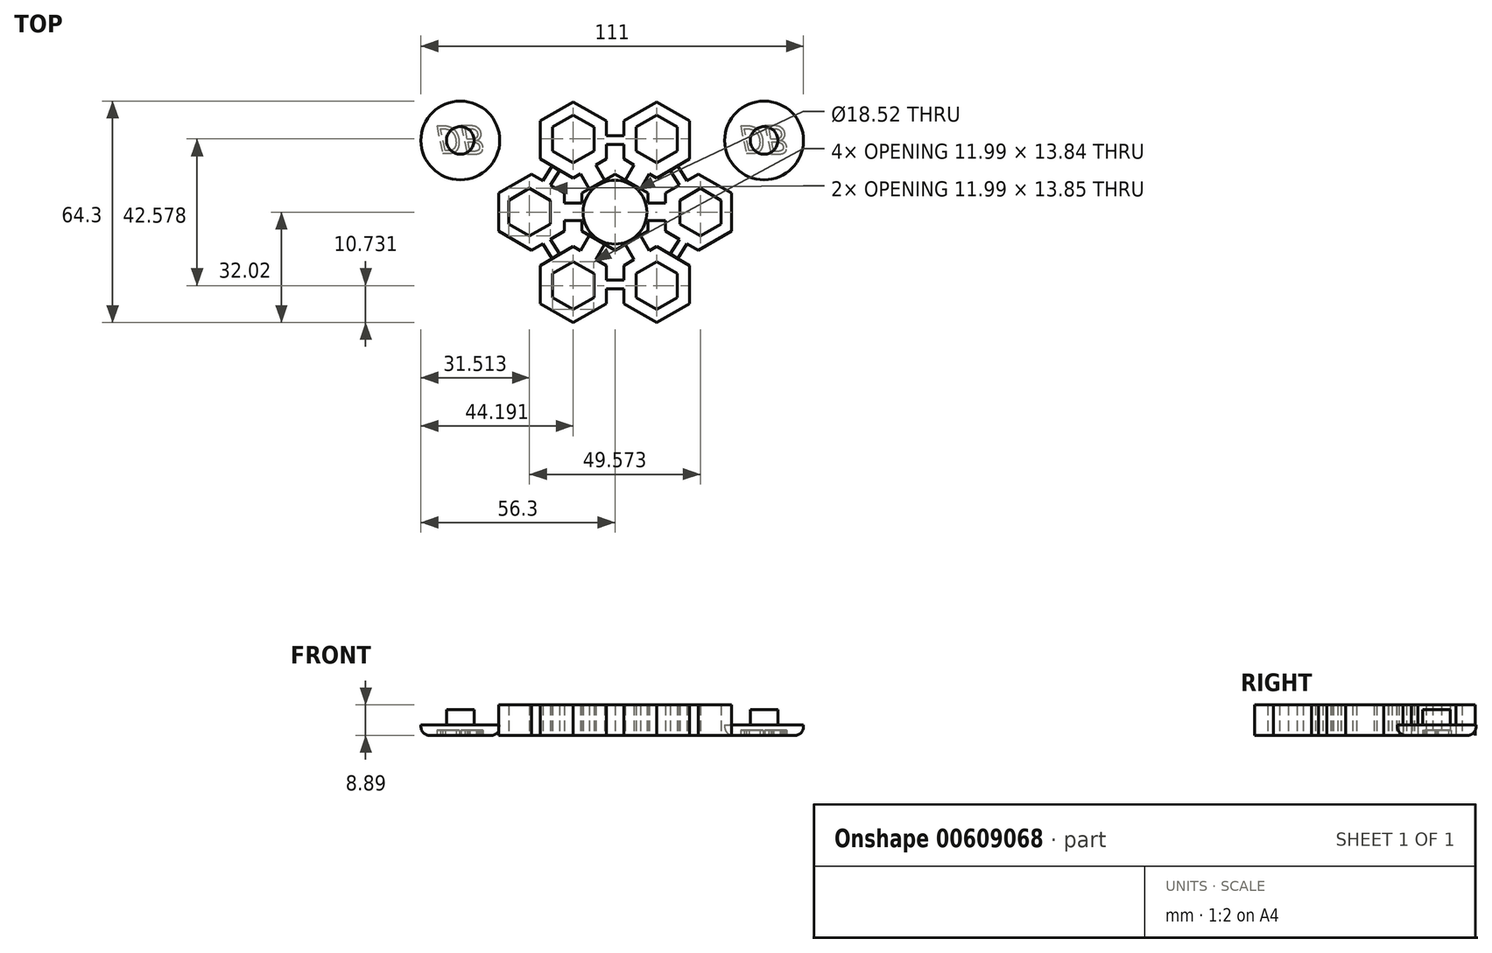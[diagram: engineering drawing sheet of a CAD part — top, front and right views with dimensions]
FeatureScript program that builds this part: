
annotation { "Feature Type Name" : "Feature", "Feature Type Description" : "" }
export const myFeature = defineFeature(function(context is Context, id is Id, definition is map)
    precondition{}
    {
        {
            var Q0;
            Q0=qCreatedBy(makeId("Top.planeOp"),FACE);
            var sketch = newSketch(context, id + "F0", { "sketchPlane" : qUnion([Q0])});
            skCircle(sketch, "E0.cCircle", {"center": v(0, 0) * mm, "radius": 9.57 * mm, "construction": true});
            skLineSegment(sketch, "E0.0", {"start": v(9.57, -5.52) * mm, "end": v(0, -11.05) * mm});
            skLineSegment(sketch, "E0.1", {"start": v(0, -11.05) * mm, "end": v(-9.57, -5.52) * mm});
            skLineSegment(sketch, "E0.2", {"start": v(-9.57, -5.52) * mm, "end": v(-9.57, 5.52) * mm});
            skLineSegment(sketch, "E0.3", {"start": v(-9.57, 5.52) * mm, "end": v(0, 11.05) * mm});
            skLineSegment(sketch, "E0.4", {"start": v(0, 11.05) * mm, "end": v(9.57, 5.52) * mm});
            skLineSegment(sketch, "E0.5", {"start": v(9.57, 5.52) * mm, "end": v(9.57, -5.52) * mm});
            skPoint(sketch, "E0.0.midPoint", {"position": v(4.78, -8.29) * mm});
            skCircle(sketch, "E1.cCircle", {"center": v(-12.1, 20.97) * mm, "radius": 9.57 * mm, "construction": true});
            skLineSegment(sketch, "E1.0", {"start": v(-2.54, 26.5) * mm, "end": v(-2.54, 15.45) * mm});
            skLineSegment(sketch, "E1.1", {"start": v(-2.54, 15.45) * mm, "end": v(-12.1, 9.92) * mm});
            skLineSegment(sketch, "E1.2", {"start": v(-12.1, 9.92) * mm, "end": v(-21.68, 15.45) * mm});
            skLineSegment(sketch, "E1.3", {"start": v(-21.68, 15.45) * mm, "end": v(-21.68, 26.5) * mm});
            skLineSegment(sketch, "E1.4", {"start": v(-21.68, 26.5) * mm, "end": v(-12.1, 32.02) * mm});
            skLineSegment(sketch, "E1.5", {"start": v(-12.1, 32.02) * mm, "end": v(-2.54, 26.5) * mm});
            skCircle(sketch, "E2.cCircle", {"center": v(-24.22, 0) * mm, "radius": 9.57 * mm, "construction": true});
            skLineSegment(sketch, "E2.0", {"start": v(-14.65, 5.52) * mm, "end": v(-14.65, -5.52) * mm});
            skLineSegment(sketch, "E2.1", {"start": v(-14.65, -5.52) * mm, "end": v(-24.22, -11.05) * mm});
            skLineSegment(sketch, "E2.2", {"start": v(-24.22, -11.05) * mm, "end": v(-33.79, -5.52) * mm});
            skLineSegment(sketch, "E2.3", {"start": v(-33.79, -5.52) * mm, "end": v(-33.79, 5.52) * mm});
            skLineSegment(sketch, "E2.4", {"start": v(-33.79, 5.52) * mm, "end": v(-24.22, 11.05) * mm});
            skLineSegment(sketch, "E2.5", {"start": v(-24.22, 11.05) * mm, "end": v(-14.65, 5.52) * mm});
            skPoint(sketch, "E2.0.midPoint", {"position": v(-14.65, 0) * mm});
            skCircle(sketch, "E3.cCircle", {"center": v(-12.1, -20.97) * mm, "radius": 9.57 * mm, "construction": true});
            skLineSegment(sketch, "E3.0", {"start": v(-2.54, -26.5) * mm, "end": v(-12.1, -32.02) * mm});
            skLineSegment(sketch, "E3.1", {"start": v(-12.1, -32.02) * mm, "end": v(-21.68, -26.5) * mm});
            skLineSegment(sketch, "E3.2", {"start": v(-21.68, -26.5) * mm, "end": v(-21.68, -15.45) * mm});
            skLineSegment(sketch, "E3.3", {"start": v(-21.68, -15.45) * mm, "end": v(-12.1, -9.92) * mm});
            skLineSegment(sketch, "E3.4", {"start": v(-12.1, -9.92) * mm, "end": v(-2.54, -15.45) * mm});
            skLineSegment(sketch, "E3.5", {"start": v(-2.54, -15.45) * mm, "end": v(-2.54, -26.5) * mm});
            skLineSegment(sketch, "E4.MirrorCS", {"start": v(21.68, 26.5) * mm, "end": v(12.1, 32.02) * mm});
            skLineSegment(sketch, "E5.MirrorCS", {"start": v(21.68, 15.45) * mm, "end": v(21.68, 26.5) * mm});
            skLineSegment(sketch, "E6.MirrorCS", {"start": v(12.1, 9.92) * mm, "end": v(21.68, 15.45) * mm});
            skLineSegment(sketch, "E7.MirrorCS", {"start": v(2.54, 15.45) * mm, "end": v(12.1, 9.92) * mm});
            skLineSegment(sketch, "E8.MirrorCS", {"start": v(2.54, 26.5) * mm, "end": v(2.54, 15.45) * mm});
            skLineSegment(sketch, "E9.MirrorCS", {"start": v(12.1, 32.02) * mm, "end": v(2.54, 26.5) * mm});
            skCircle(sketch, "E10.MirrorC", {"center": v(12.1, 20.97) * mm, "radius": 9.57 * mm, "construction": true});
            skLineSegment(sketch, "E11.MirrorCS", {"start": v(24.22, 11.05) * mm, "end": v(14.65, 5.52) * mm});
            skLineSegment(sketch, "E12.MirrorCS", {"start": v(33.79, 5.52) * mm, "end": v(24.22, 11.05) * mm});
            skLineSegment(sketch, "E13.MirrorCS", {"start": v(33.79, -5.52) * mm, "end": v(33.79, 5.52) * mm});
            skLineSegment(sketch, "E14.MirrorCS", {"start": v(24.22, -11.05) * mm, "end": v(33.79, -5.52) * mm});
            skLineSegment(sketch, "E15.MirrorCS", {"start": v(14.65, -5.52) * mm, "end": v(24.22, -11.05) * mm});
            skLineSegment(sketch, "E16.MirrorCS", {"start": v(14.65, 5.52) * mm, "end": v(14.65, -5.52) * mm});
            skCircle(sketch, "E17.MirrorC", {"center": v(24.22, 0) * mm, "radius": 9.57 * mm, "construction": true});
            skLineSegment(sketch, "E18.MirrorCS", {"start": v(2.54, -15.45) * mm, "end": v(2.54, -26.5) * mm});
            skLineSegment(sketch, "E19.MirrorCS", {"start": v(12.1, -9.92) * mm, "end": v(2.54, -15.45) * mm});
            skLineSegment(sketch, "E20.MirrorCS", {"start": v(21.68, -15.45) * mm, "end": v(12.1, -9.92) * mm});
            skLineSegment(sketch, "E21.MirrorCS", {"start": v(21.68, -26.5) * mm, "end": v(21.68, -15.45) * mm});
            skLineSegment(sketch, "E22.MirrorCS", {"start": v(12.1, -32.02) * mm, "end": v(21.68, -26.5) * mm});
            skLineSegment(sketch, "E23.MirrorCS", {"start": v(2.54, -26.5) * mm, "end": v(12.1, -32.02) * mm});
            skCircle(sketch, "E24.MirrorC", {"center": v(12.1, -20.97) * mm, "radius": 9.57 * mm, "construction": true});
            skLineSegment(sketch, "E25.bottom", {"start": v(-14.65, 2.67) * mm, "end": v(-9.57, 2.67) * mm});
            skLineSegment(sketch, "E25.top", {"start": v(-14.65, -2.41) * mm, "end": v(-9.57, -2.41) * mm});
            skLineSegment(sketch, "E25.left", {"start": v(-14.65, 2.67) * mm, "end": v(-14.65, -2.41) * mm});
            skLineSegment(sketch, "E25.right", {"start": v(-9.57, 2.67) * mm, "end": v(-9.57, -2.41) * mm});
            skLineSegment(sketch, "E26.MirrorCS", {"start": v(14.65, 2.67) * mm, "end": v(9.57, 2.67) * mm});
            skLineSegment(sketch, "E27.MirrorCS", {"start": v(14.65, -2.41) * mm, "end": v(9.57, -2.41) * mm});
            skLineSegment(sketch, "E28.MirrorCS", {"start": v(9.57, 2.67) * mm, "end": v(9.57, -2.41) * mm});
            skLineSegment(sketch, "E29.bottom", {"start": v(-9.96, 11.17) * mm, "end": v(-5.56, 13.7) * mm});
            skLineSegment(sketch, "E29.top", {"start": v(-7.42, 6.77) * mm, "end": v(-3.02, 9.3) * mm});
            skLineSegment(sketch, "E29.left", {"start": v(-9.96, 11.17) * mm, "end": v(-7.42, 6.77) * mm});
            skLineSegment(sketch, "E29.right", {"start": v(-5.56, 13.7) * mm, "end": v(-3.02, 9.3) * mm});
            skLineSegment(sketch, "E30.MirrorCS", {"start": v(-9.57, -5.52) * mm, "end": v(0, -11.05) * mm});
            skLineSegment(sketch, "E31.bottom", {"start": v(-2.54, -19.7) * mm, "end": v(2.54, -19.7) * mm});
            skLineSegment(sketch, "E31.top", {"start": v(-2.54, -22.24) * mm, "end": v(2.54, -22.24) * mm});
            skLineSegment(sketch, "E31.left", {"start": v(-2.54, -19.7) * mm, "end": v(-2.54, -22.24) * mm});
            skLineSegment(sketch, "E31.right", {"start": v(2.54, -19.7) * mm, "end": v(2.54, -22.24) * mm});
            skLineSegment(sketch, "E32.MirrorCS", {"start": v(9.96, 11.17) * mm, "end": v(7.42, 6.77) * mm});
            skLineSegment(sketch, "E33.MirrorCS", {"start": v(9.96, 11.17) * mm, "end": v(5.56, 13.7) * mm});
            skLineSegment(sketch, "E34.MirrorCS", {"start": v(5.56, 13.7) * mm, "end": v(3.02, 9.3) * mm});
            skLineSegment(sketch, "E35.MirrorCS", {"start": v(9.57, 5.52) * mm, "end": v(0, 11.05) * mm});
            skLineSegment(sketch, "E36", {"start": v(3.02, 9.3) * mm, "end": v(7.42, 6.77) * mm});
            skLineSegment(sketch, "E37.MirrorCS", {"start": v(-9.96, -11.17) * mm, "end": v(-7.42, -6.77) * mm});
            skLineSegment(sketch, "E38.MirrorCS", {"start": v(-5.56, -13.7) * mm, "end": v(-3.02, -9.3) * mm});
            skLineSegment(sketch, "E39.MirrorCS", {"start": v(-9.96, -11.17) * mm, "end": v(-5.56, -13.7) * mm});
            skLineSegment(sketch, "E40.MirrorCS", {"start": v(-7.42, -6.77) * mm, "end": v(-3.02, -9.3) * mm});
            skLineSegment(sketch, "E41.MirrorCS", {"start": v(9.96, -11.17) * mm, "end": v(7.42, -6.77) * mm});
            skLineSegment(sketch, "E42.MirrorCS", {"start": v(5.56, -13.7) * mm, "end": v(3.02, -9.3) * mm});
            skLineSegment(sketch, "E43", {"start": v(5.56, 13.7) * mm, "end": v(9.96, 11.17) * mm});
            skLineSegment(sketch, "E44.MirrorCS", {"start": v(5.56, -13.7) * mm, "end": v(9.96, -11.17) * mm});
            skLineSegment(sketch, "E45", {"start": v(3.02, -9.3) * mm, "end": v(7.42, -6.77) * mm});
            skLineSegment(sketch, "E46.MirrorCS", {"start": v(-2.54, 19.7) * mm, "end": v(2.54, 19.7) * mm});
            skLineSegment(sketch, "E47.MirrorCS", {"start": v(2.54, 19.7) * mm, "end": v(2.54, 22.24) * mm});
            skLineSegment(sketch, "E48.MirrorCS", {"start": v(-2.54, 19.7) * mm, "end": v(-2.54, 22.24) * mm});
            skLineSegment(sketch, "E49.MirrorCS", {"start": v(-2.54, 22.24) * mm, "end": v(2.54, 22.24) * mm});
            skLineSegment(sketch, "E50.bottom", {"start": v(-20.9, 9.14) * mm, "end": v(-18.21, 13.44) * mm});
            skLineSegment(sketch, "E50.top", {"start": v(-18.76, 7.79) * mm, "end": v(-16.06, 12.1) * mm});
            skLineSegment(sketch, "E50.left", {"start": v(-20.9, 9.14) * mm, "end": v(-18.76, 7.79) * mm});
            skLineSegment(sketch, "E50.right", {"start": v(-18.21, 13.44) * mm, "end": v(-16.06, 12.1) * mm});
            skLineSegment(sketch, "E51.0", {"start": v(-20.9, 9.14) * mm, "end": v(-18.21, 13.44) * mm, "construction": true});
            skLineSegment(sketch, "E51.1", {"start": v(-20.9, 9.14) * mm, "end": v(-20.9, 9.14) * mm});
            skLineSegment(sketch, "E52.MirrorCS", {"start": v(20.9, 9.14) * mm, "end": v(18.21, 13.44) * mm});
            skLineSegment(sketch, "E53.MirrorCS", {"start": v(18.21, 13.44) * mm, "end": v(16.06, 12.1) * mm});
            skLineSegment(sketch, "E54.MirrorCS", {"start": v(18.76, 7.79) * mm, "end": v(16.06, 12.1) * mm});
            skLineSegment(sketch, "E55.MirrorCS", {"start": v(20.9, 9.14) * mm, "end": v(18.76, 7.79) * mm});
            skLineSegment(sketch, "E56.MirrorCS", {"start": v(-20.9, -9.14) * mm, "end": v(-18.21, -13.44) * mm});
            skLineSegment(sketch, "E57.MirrorCS", {"start": v(-18.76, -7.79) * mm, "end": v(-16.06, -12.1) * mm});
            skLineSegment(sketch, "E58.MirrorCS", {"start": v(-18.21, -13.44) * mm, "end": v(-16.06, -12.1) * mm});
            skLineSegment(sketch, "E59.MirrorCS", {"start": v(-20.9, -9.14) * mm, "end": v(-18.76, -7.79) * mm});
            skLineSegment(sketch, "E60.MirrorCS", {"start": v(18.76, -7.79) * mm, "end": v(16.06, -12.1) * mm});
            skLineSegment(sketch, "E61.MirrorCS", {"start": v(20.9, -9.14) * mm, "end": v(18.76, -7.79) * mm});
            skLineSegment(sketch, "E62.MirrorCS", {"start": v(20.9, -9.14) * mm, "end": v(18.21, -13.44) * mm});
            skLineSegment(sketch, "E63.MirrorCS", {"start": v(18.21, -13.44) * mm, "end": v(16.06, -12.1) * mm});
            skCircle(sketch, "E64", {"center": v(0, 0) * mm, "radius": 9.26 * mm});
            skSolve(sketch);
        }
        {
            var Q0;
            Q0 = qSketchRegion(id + "F0", true);
            extrude(context, id + "F1", {"entities" : qUnion([Q0]), "depth" : 8.9 * mm, "offsetDistance" : 25.4 * mm});
        }
        {
            var Q0;
            Q0=makeQuery(id+"F1.opExtrude","CAP_FACE",FACE,{"disambiguationData":[OSD([sQuery(id+"F0.wireOp",EDGE,"E0.0"),sQuery(id+"F0.wireOp",EDGE,"E0.2"),sQuery(id+"F0.wireOp",EDGE,"E0.3"),sQuery(id+"F0.wireOp",EDGE,"E0.5"),sQuery(id+"F0.wireOp",EDGE,"E2.0"),sQuery(id+"F0.wireOp",EDGE,"E2.1"),sQuery(id+"F0.wireOp",EDGE,"E2.2"),sQuery(id+"F0.wireOp",EDGE,"E2.3"),sQuery(id+"F0.wireOp",EDGE,"E2.4"),sQuery(id+"F0.wireOp",EDGE,"E2.5"),sQuery(id+"F0.wireOp",EDGE,"E12.MirrorCS"),sQuery(id+"F0.wireOp",EDGE,"E13.MirrorCS"),sQuery(id+"F0.wireOp",EDGE,"E14.MirrorCS"),sQuery(id+"F0.wireOp",EDGE,"E15.MirrorCS"),sQuery(id+"F0.wireOp",EDGE,"E16.MirrorCS"),sQuery(id+"F0.wireOp",EDGE,"E11.MirrorCS"),sQuery(id+"F0.wireOp",EDGE,"E25.bottom"),sQuery(id+"F0.wireOp",EDGE,"E25.top"),sQuery(id+"F0.wireOp",EDGE,"E26.MirrorCS"),sQuery(id+"F0.wireOp",EDGE,"E27.MirrorCS"),sQuery(id+"F0.wireOp",EDGE,"E30.MirrorCS"),sQuery(id+"F0.wireOp",EDGE,"E35.MirrorCS"),sQuery(id+"F0.wireOp",EDGE,"E50.bottom"),sQuery(id+"F0.wireOp",EDGE,"E50.top"),sQuery(id+"F0.wireOp",EDGE,"E50.right"),sQuery(id+"F0.wireOp",EDGE,"E52.MirrorCS"),sQuery(id+"F0.wireOp",EDGE,"E53.MirrorCS"),sQuery(id+"F0.wireOp",EDGE,"E54.MirrorCS"),sQuery(id+"F0.wireOp",EDGE,"E56.MirrorCS"),sQuery(id+"F0.wireOp",EDGE,"E57.MirrorCS"),sQuery(id+"F0.wireOp",EDGE,"E58.MirrorCS"),sQuery(id+"F0.wireOp",EDGE,"E60.MirrorCS"),sQuery(id+"F0.wireOp",EDGE,"E62.MirrorCS"),sQuery(id+"F0.wireOp",EDGE,"E63.MirrorCS"),sQuery(id+"F0.wireOp",EDGE,"E64")])],"isStart":true});
            var sketch = newSketch(context, id + "F2", { "sketchPlane" : qUnion([Q0])});
            skCircle(sketch, "E65.cCircle", {"center": v(-24.79, 0) * mm, "radius": 6 * mm, "construction": true});
            skLineSegment(sketch, "E65.0", {"start": v(-18.8, 3.46) * mm, "end": v(-18.8, -3.46) * mm});
            skLineSegment(sketch, "E65.1", {"start": v(-18.8, -3.46) * mm, "end": v(-24.79, -6.92) * mm});
            skLineSegment(sketch, "E65.2", {"start": v(-24.79, -6.92) * mm, "end": v(-30.78, -3.46) * mm});
            skLineSegment(sketch, "E65.3", {"start": v(-30.78, -3.46) * mm, "end": v(-30.78, 3.46) * mm});
            skLineSegment(sketch, "E65.4", {"start": v(-30.78, 3.46) * mm, "end": v(-24.79, 6.92) * mm});
            skLineSegment(sketch, "E65.5", {"start": v(-24.79, 6.92) * mm, "end": v(-18.8, 3.46) * mm});
            skPoint(sketch, "E65.0.midPoint", {"position": v(-18.8, 0) * mm});
            skLineSegment(sketch, "E66.MirrorCS", {"start": v(24.79, 6.92) * mm, "end": v(18.8, 3.46) * mm});
            skLineSegment(sketch, "E67.MirrorCS", {"start": v(30.78, 3.46) * mm, "end": v(24.79, 6.92) * mm});
            skLineSegment(sketch, "E68.MirrorCS", {"start": v(18.8, 3.46) * mm, "end": v(18.8, -3.46) * mm});
            skLineSegment(sketch, "E69.MirrorCS", {"start": v(18.8, -3.46) * mm, "end": v(24.79, -6.92) * mm});
            skLineSegment(sketch, "E70.MirrorCS", {"start": v(24.79, -6.92) * mm, "end": v(30.78, -3.46) * mm});
            skLineSegment(sketch, "E71.MirrorCS", {"start": v(30.78, -3.46) * mm, "end": v(30.78, 3.46) * mm});
            skCircle(sketch, "E72.MirrorC", {"center": v(24.79, 0) * mm, "radius": 6 * mm, "construction": true});
            skCircle(sketch, "E73.cCircle", {"center": v(-12.1, 21.29) * mm, "radius": 6 * mm, "construction": true});
            skLineSegment(sketch, "E73.0", {"start": v(-6.11, 24.75) * mm, "end": v(-6.11, 17.83) * mm});
            skLineSegment(sketch, "E73.1", {"start": v(-6.11, 17.83) * mm, "end": v(-12.1, 14.37) * mm});
            skLineSegment(sketch, "E73.2", {"start": v(-12.1, 14.37) * mm, "end": v(-18.1, 17.83) * mm});
            skLineSegment(sketch, "E73.3", {"start": v(-18.1, 17.83) * mm, "end": v(-18.1, 24.75) * mm});
            skLineSegment(sketch, "E73.4", {"start": v(-18.1, 24.75) * mm, "end": v(-12.1, 28.21) * mm});
            skLineSegment(sketch, "E73.5", {"start": v(-12.1, 28.21) * mm, "end": v(-6.11, 24.75) * mm});
            skPoint(sketch, "E73.0.midPoint", {"position": v(-38.14, 21.4) * mm});
            skCircle(sketch, "E74.MirrorC", {"center": v(12.1, 21.29) * mm, "radius": 6 * mm, "construction": true});
            skLineSegment(sketch, "E75.MirrorCS", {"start": v(18.1, 24.75) * mm, "end": v(12.1, 28.21) * mm});
            skLineSegment(sketch, "E76.MirrorCS", {"start": v(12.1, 28.21) * mm, "end": v(6.11, 24.75) * mm});
            skLineSegment(sketch, "E77.MirrorCS", {"start": v(6.11, 24.75) * mm, "end": v(6.11, 17.83) * mm});
            skLineSegment(sketch, "E78.MirrorCS", {"start": v(6.11, 17.83) * mm, "end": v(12.1, 14.37) * mm});
            skLineSegment(sketch, "E79.MirrorCS", {"start": v(12.1, 14.37) * mm, "end": v(18.1, 17.83) * mm});
            skLineSegment(sketch, "E80.MirrorCS", {"start": v(18.1, 17.83) * mm, "end": v(18.1, 24.75) * mm});
            skLineSegment(sketch, "E81.MirrorCS", {"start": v(-12.1, -14.37) * mm, "end": v(-18.1, -17.83) * mm});
            skCircle(sketch, "E82.MirrorC", {"center": v(-12.1, -21.29) * mm, "radius": 6 * mm, "construction": true});
            skLineSegment(sketch, "E83.MirrorCS", {"start": v(-6.11, -17.83) * mm, "end": v(-12.1, -14.37) * mm});
            skLineSegment(sketch, "E84.MirrorCS", {"start": v(-6.11, -24.75) * mm, "end": v(-6.11, -17.83) * mm});
            skLineSegment(sketch, "E85.MirrorCS", {"start": v(-12.1, -28.21) * mm, "end": v(-6.11, -24.75) * mm});
            skLineSegment(sketch, "E86.MirrorCS", {"start": v(-18.1, -24.75) * mm, "end": v(-12.1, -28.21) * mm});
            skLineSegment(sketch, "E87.MirrorCS", {"start": v(-18.1, -17.83) * mm, "end": v(-18.1, -24.75) * mm});
            skCircle(sketch, "E88.MirrorC", {"center": v(12.1, -21.29) * mm, "radius": 6 * mm, "construction": true});
            skLineSegment(sketch, "E89.MirrorCS", {"start": v(6.11, -17.83) * mm, "end": v(12.1, -14.37) * mm});
            skLineSegment(sketch, "E90.MirrorCS", {"start": v(12.1, -14.37) * mm, "end": v(18.1, -17.83) * mm});
            skLineSegment(sketch, "E91.MirrorCS", {"start": v(18.1, -17.83) * mm, "end": v(18.1, -24.75) * mm});
            skLineSegment(sketch, "E92.MirrorCS", {"start": v(18.1, -24.75) * mm, "end": v(12.1, -28.21) * mm});
            skLineSegment(sketch, "E93.MirrorCS", {"start": v(12.1, -28.21) * mm, "end": v(6.11, -24.75) * mm});
            skLineSegment(sketch, "E94.MirrorCS", {"start": v(6.11, -24.75) * mm, "end": v(6.11, -17.83) * mm});
            skSolve(sketch);
        }
        {
            var Q0;
            Q0=makeQuery(id+"F2.imprint","IMPRINT",FACE,{"disambiguationData":[TD([[makeQuery(id+"F2.imprint","IMPRINT",EDGE,{"derivedFrom":sQuery(id+"F2.wireOp",EDGE,"E73.0")}),-1.0]])]});
            var Q1;
            Q1=makeQuery(id+"F2.imprint","IMPRINT",FACE,{"disambiguationData":[TD([[makeQuery(id+"F2.imprint","IMPRINT",EDGE,{"derivedFrom":sQuery(id+"F2.wireOp",EDGE,"E75.MirrorCS")}),1.0]])]});
            var Q2;
            Q2=makeQuery(id+"F2.imprint","IMPRINT",FACE,{"disambiguationData":[TD([[makeQuery(id+"F2.imprint","IMPRINT",EDGE,{"derivedFrom":sQuery(id+"F2.wireOp",EDGE,"E66.MirrorCS")}),1.0]])]});
            var Q3;
            Q3=makeQuery(id+"F2.imprint","IMPRINT",FACE,{"disambiguationData":[TD([[makeQuery(id+"F2.imprint","IMPRINT",EDGE,{"derivedFrom":sQuery(id+"F2.wireOp",EDGE,"E65.0")}),-1.0]])]});
            var Q4;
            Q4=makeQuery(id+"F2.imprint","IMPRINT",FACE,{"disambiguationData":[TD([[makeQuery(id+"F2.imprint","IMPRINT",EDGE,{"derivedFrom":sQuery(id+"F2.wireOp",EDGE,"E81.MirrorCS")}),1.0]])]});
            var Q5;
            Q5=makeQuery(id+"F2.imprint","IMPRINT",FACE,{"disambiguationData":[TD([[makeQuery(id+"F2.imprint","IMPRINT",EDGE,{"derivedFrom":sQuery(id+"F2.wireOp",EDGE,"E89.MirrorCS")}),-1.0]])]});
            extrude(context, id + "F3", {"entities" : qUnion([Q0, Q1, Q2, Q3, Q4, Q5]), "operationType" : NewBodyOperationType.REMOVE, "oppositeDirection" : true, "depth" : 8.9 * mm, "offsetDistance" : 25.4 * mm});
        }
        {
            var Q0;
            Q0=qCreatedBy(makeId("Top.planeOp"),FACE);
            var sketch = newSketch(context, id + "F4", { "sketchPlane" : qUnion([Q0])});
            skCircle(sketch, "E95", {"center": v(43.27, 20.85) * mm, "radius": 11.43 * mm});
            skSolve(sketch);
        }
        {
            var Q0;
            Q0=makeQuery(id+"F4.imprint","IMPRINT",FACE,{"disambiguationData":[TD([[makeQuery(id+"F4.imprint","IMPRINT",EDGE,{"derivedFrom":sQuery(id+"F4.wireOp",EDGE,"E95")}),1.0]])]});
            extrude(context, id + "F5", {"entities" : qUnion([Q0]), "depth" : 3.05 * mm, "offsetDistance" : 25.4 * mm});
        }
        {
            var Q0;
            Q0=makeQuery(id+"F5.opExtrude","CAP_FACE",FACE,{"disambiguationData":[OSD([sQuery(id+"F4.wireOp",EDGE,"E95")])],"isStart":false});
            var sketch = newSketch(context, id + "F6", { "sketchPlane" : qUnion([Q0])});
            skCircle(sketch, "E96", {"center": v(43.27, 20.85) * mm, "radius": 4 * mm});
            skSolve(sketch);
        }
        {
            var Q0;
            Q0=makeQuery(id+"F6.imprint","IMPRINT",FACE,{"disambiguationData":[TD([[makeQuery(id+"F6.imprint","IMPRINT",EDGE,{"derivedFrom":sQuery(id+"F6.wireOp",EDGE,"E96")}),1.0]])]});
            extrude(context, id + "F7", {"entities" : qUnion([Q0]), "operationType" : NewBodyOperationType.ADD, "depth" : 4.44 * mm, "offsetDistance" : 25.4 * mm});
        }
        {
            var Q0;
            Q0=makeQuery(id+"F5.opExtrude","CAP_EDGE",EDGE,{"disambiguationData":[OSD([sQuery(id+"F4.wireOp",EDGE,"E95")])],"isStart":true});
            fillet(context, id + "F8", {"entities" : qUnion([Q0]), "radius" : 2.54 * mm, "tangentPropagation" : true, "allowEdgeOverflow" : false});
        }
        {
            var Q0;
            Q0=makeQuery(id+"F5.opExtrude","CAP_FACE",FACE,{"disambiguationData":[OSD([sQuery(id+"F4.wireOp",EDGE,"E95")])],"isStart":true});
            var sketch = newSketch(context, id + "F9", { "sketchPlane" : qUnion([Q0])});
            skText(sketch, "E97", { "text": "B", "fontName": "OpenSans-Italic.ttf"});
            const initialGuessF9  = {"E97": [0.04304, -0.02511, 1, 0, 0.00832]};
            skSetInitialGuess(sketch, initialGuessF9);
            skSolve(sketch);
        }
        {
            var Q0;
            Q0 = qSketchRegion(id + "F9", true);
            extrude(context, id + "F10", {"entities" : qUnion([Q0]), "operationType" : NewBodyOperationType.REMOVE, "oppositeDirection" : true, "depth" : 1.52 * mm, "offsetDistance" : 25.4 * mm});
        }
        {
            var Q0;
            {var subQ0=sQuery(id+"F4.wireOp",EDGE,"E95");Q0=makeQuery(id+"F10.boolean.opBoolean","SPLIT",FACE,{"disambiguationData":[TD([makeQuery(id+"F8.opFillet","BLEND_FACE",FACE,{"disambiguationData":[OSD([subQ0])]})])],"derivedFrom":makeQuery(id+"F5.opExtrude","CAP_FACE",FACE,{"disambiguationData":[OSD([subQ0])],"isStart":true})});}
            var sketch = newSketch(context, id + "F11", { "sketchPlane" : qUnion([Q0])});
            skText(sketch, "E98", { "text": "D", "fontName": "OpenSans-Italic.ttf"});
            const initialGuessF11  = {"E98": [0.03597, -0.02503, 1, 0, 0.00797]};
            skSetInitialGuess(sketch, initialGuessF11);
            skSolve(sketch);
        }
        {
            var Q0;
            Q0 = qSketchRegion(id + "F11", true);
            extrude(context, id + "F12", {"entities" : qUnion([Q0]), "operationType" : NewBodyOperationType.REMOVE, "oppositeDirection" : true, "depth" : 1.52 * mm, "offsetDistance" : 25.4 * mm});
        }
        {
            var Q0;
            Q0=makeQuery(id+"F5.opExtrude","SWEPT_BODY",BODY,{"disambiguationData":[OSD([sQuery(id+"F4.wireOp",EDGE,"E95")])]});
            transform(context, id + "F13", {"entities" : qUnion([Q0]), "transformType" : TransformType.TRANSLATION_3D, "dx" : -88.14 * mm, "dy" : 0 * mm, "dz" : 0 * mm, "makeCopy" : true});
        }
    });
